annotation { "Feature Type Name" : "Feature", "Feature Type Description" : "" }
export const myFeature = defineFeature(function(context is Context, id is Id, definition is map)
    precondition{}
    {
        {
            var Q0;
            Q0=qCreatedBy(makeId("Top.planeOp"),FACE);
            var sketch = newSketch(context, id + "F0", { "sketchPlane" : qUnion([Q0])});
            skCircle(sketch, "E0", {"center": v(0, 0) * mm, "radius": 38.1 * mm});
            skSolve(sketch);
        }
        {
            var Q0;
            Q0 = qSketchRegion(id + "F0", true);
            extrude(context, id + "F1", {"entities" : qUnion([Q0]), "oppositeDirection" : true, "depth" : 3.8 * mm});
        }
        {
            var Q0;
            Q0=makeQuery(id+"F0.imprint","IMPRINT",FACE,{"disambiguationData":[TD([[makeQuery(id+"F0.imprint","IMPRINT",EDGE,{"derivedFrom":sQuery(id+"F0.wireOp",EDGE,"E0")}),1.0]])]});
            var sketch = newSketch(context, id + "F2", { "sketchPlane" : qUnion([Q0])});
            skLineSegment(sketch, "E1", {"start": v(0, 0) * mm, "end": v(0, -3.81) * mm});
            skLineSegment(sketch, "E2", {"start": v(0, -3.81) * mm, "end": v(-5.08, -8.9) * mm});
            skLineSegment(sketch, "E3", {"start": v(-5.08, -8.9) * mm, "end": v(-8.46, -8.9) * mm});
            skLineSegment(sketch, "E4", {"start": v(-20.32, -8.9) * mm, "end": v(-25.4, -3.81) * mm});
            skLineSegment(sketch, "E5", {"start": v(-25.4, -3.81) * mm, "end": v(-25.4, 0) * mm});
            skLineSegment(sketch, "E6", {"start": v(-25.4, 0) * mm, "end": v(-25.4, 11.43) * mm});
            skLineSegment(sketch, "E7", {"start": v(-25.4, 11.43) * mm, "end": v(-20.32, 16.5) * mm});
            skLineSegment(sketch, "E8", {"start": v(-20.32, 16.5) * mm, "end": v(-5.08, 16.5) * mm});
            skLineSegment(sketch, "E9", {"start": v(-5.08, 16.5) * mm, "end": v(0, 11.43) * mm});
            skLineSegment(sketch, "E10", {"start": v(0, 11.43) * mm, "end": v(0, 7.62) * mm});
            skLineSegment(sketch, "E11", {"start": v(0, 7.62) * mm, "end": v(-5.08, 7.62) * mm});
            skLineSegment(sketch, "E12", {"start": v(-5.08, 7.62) * mm, "end": v(-5.08, 11.43) * mm});
            skLineSegment(sketch, "E13", {"start": v(-5.08, 11.43) * mm, "end": v(-20.32, 11.43) * mm});
            skLineSegment(sketch, "E14", {"start": v(-20.32, 11.43) * mm, "end": v(-20.32, -3.81) * mm});
            skLineSegment(sketch, "E15", {"start": v(-20.32, -3.81) * mm, "end": v(-13.97, -3.81) * mm});
            skLineSegment(sketch, "E16", {"start": v(-5.08, -3.81) * mm, "end": v(-5.08, 0) * mm});
            skLineSegment(sketch, "E17", {"start": v(-5.08, 0) * mm, "end": v(0, 0) * mm});
            skLineSegment(sketch, "E18", {"start": v(-8.9, 5.08) * mm, "end": v(-13.97, 5.08) * mm});
            skLineSegment(sketch, "E19", {"start": v(-17.78, 5.08) * mm, "end": v(-17.78, 0) * mm});
            skLineSegment(sketch, "E20", {"start": v(-17.78, 0) * mm, "end": v(-13.97, 0) * mm});
            skLineSegment(sketch, "E21", {"start": v(-13.97, 0) * mm, "end": v(-13.97, -3.81) * mm});
            skLineSegment(sketch, "E22", {"start": v(-8.9, 5.08) * mm, "end": v(-8.9, -3.81) * mm});
            skLineSegment(sketch, "E23.trimOffspring", {"start": v(-8.9, -3.81) * mm, "end": v(-5.08, -3.81) * mm});
            skLineSegment(sketch, "E24", {"start": v(-8.46, -8.9) * mm, "end": v(-8.46, -16.52) * mm});
            skLineSegment(sketch, "E25", {"start": v(-8.46, -16.52) * mm, "end": v(6.78, -16.52) * mm});
            skLineSegment(sketch, "E26", {"start": v(6.78, -16.52) * mm, "end": v(6.78, 5.07) * mm});
            skLineSegment(sketch, "E27", {"start": v(6.78, 5.07) * mm, "end": v(14.4, 5.07) * mm});
            skLineSegment(sketch, "E28", {"start": v(14.4, 5.07) * mm, "end": v(14.4, 0) * mm});
            skLineSegment(sketch, "E29", {"start": v(14.4, 0) * mm, "end": v(11.86, 0) * mm});
            skLineSegment(sketch, "E30", {"start": v(11.86, 0) * mm, "end": v(11.86, -16.52) * mm});
            skLineSegment(sketch, "E31", {"start": v(11.86, -16.52) * mm, "end": v(6.78, -21.6) * mm});
            skLineSegment(sketch, "E32", {"start": v(6.78, -21.6) * mm, "end": v(-8.46, -21.6) * mm});
            skLineSegment(sketch, "E33", {"start": v(-8.46, -21.6) * mm, "end": v(-13.54, -16.52) * mm});
            skLineSegment(sketch, "E34", {"start": v(-13.54, -16.52) * mm, "end": v(-13.54, -8.9) * mm});
            skLineSegment(sketch, "E35", {"start": v(-13.97, 5.08) * mm, "end": v(-17.78, 5.08) * mm});
            skCircle(sketch, "E36", {"center": v(0, 0) * mm, "radius": 34.93 * mm});
            skLineSegment(sketch, "E37.trimOffspring", {"start": v(-13.54, -8.9) * mm, "end": v(-20.32, -8.9) * mm});
            skText(sketch, "E38", { "text": "P", "fontName": "OpenSans-Regular.ttf"});
            skText(sketch, "E39", { "text": "C", "fontName": "OpenSans-Regular.ttf"});
            skText(sketch, "E40", { "text": "D", "fontName": "OpenSans-Regular.ttf"});
            skText(sketch, "E41", { "text": "P\n", "fontName": "OpenSans-Regular.ttf"});
            const initialGuessF2  = {"E38": [0.00385, 0.01917, 1, 0, 0.00762], "E39": [0.00554, 0.0141, 1, 0, 0.00762], "E40": [0.0099, 0.00647, 1, 0, 0.00762], "E41": [0.0139, -0.00203, 1, 0, 0.00762]};
            skSetInitialGuess(sketch, initialGuessF2);
            skSolve(sketch);
        }
        {
            var Q0;
            Q0=makeQuery(id+"F2.imprint","IMPRINT",FACE,{"disambiguationData":[TD([[makeQuery(id+"F2.imprint","IMPRINT",EDGE,{"derivedFrom":sQuery(id+"F2.wireOp",EDGE,"E36")}),-1.0]])]});
            var Q1;
            Q1=makeQuery(id+"F2.imprint","IMPRINT",FACE,{"disambiguationData":[TD([[makeQuery(id+"F2.imprint","IMPRINT",EDGE,{"derivedFrom":sQuery(id+"F2.wireOp",EDGE,"E1")}),-1.0]])]});
            var Q2;
            Q2=makeQuery(id+"F2.imprint","IMPRINT",FACE,{"disambiguationData":[TD([[makeQuery(id+"F2.imprint","IMPRINT",EDGE,{"derivedFrom":sQuery(id+"F2.wireOp",EDGE,"E38.sketch_text.stroke-0")}),-1.0]])]});
            var Q3;
            Q3=makeQuery(id+"F2.imprint","IMPRINT",FACE,{"disambiguationData":[TD([[makeQuery(id+"F2.imprint","IMPRINT",EDGE,{"derivedFrom":sQuery(id+"F2.wireOp",EDGE,"E39.sketch_text.stroke-0")}),-1.0]])]});
            var Q4;
            Q4=makeQuery(id+"F2.imprint","IMPRINT",FACE,{"disambiguationData":[TD([[makeQuery(id+"F2.imprint","IMPRINT",EDGE,{"derivedFrom":sQuery(id+"F2.wireOp",EDGE,"E40.sketch_text.stroke-0")}),-1.0]])]});
            var Q5;
            Q5=makeQuery(id+"F2.imprint","IMPRINT",FACE,{"disambiguationData":[TD([[makeQuery(id+"F2.imprint","IMPRINT",EDGE,{"derivedFrom":sQuery(id+"F2.wireOp",EDGE,"E41.sketch_text.stroke-0")}),-1.0]])]});
            extrude(context, id + "F3", {"entities" : qUnion([Q0, Q1, Q2, Q3, Q4, Q5]), "depth" : 0.64 * mm});
        }
        {
            var Q0;
            Q0=makeQuery(id+"F1.opExtrude","CAP_FACE",FACE,{"disambiguationData":[OSD([sQuery(id+"F0.wireOp",EDGE,"E0")])],"isStart":false});
            var sketch = newSketch(context, id + "F4", { "sketchPlane" : qUnion([Q0])});
            skText(sketch, "E42", { "text": "Edi Rivas", "fontName": "OpenSans-Bold.ttf"});
            skText(sketch, "E43", { "text": "2016", "fontName": "OpenSans-Bold.ttf"});
            skCircle(sketch, "E44", {"center": v(0, 0) * mm, "radius": 34.93 * mm});
            const initialGuessF4  = {"E42": [-0.01366, 0.0027, 1, 0, 0.0062], "E43": [-0.0086, -0.009, 1, 0, 0.0079]};
            skSetInitialGuess(sketch, initialGuessF4);
            skSolve(sketch);
        }
        {
            var Q0;
            Q0=makeQuery(id+"F4.imprint","IMPRINT",FACE,{"disambiguationData":[TD([[makeQuery(id+"F4.imprint","IMPRINT",EDGE,{"derivedFrom":sQuery(id+"F4.wireOp",EDGE,"E42.sketch_text.stroke-0")}),-1.0]])]});
            var Q1;
            Q1=makeQuery(id+"F4.imprint","IMPRINT",FACE,{"disambiguationData":[TD([[makeQuery(id+"F4.imprint","IMPRINT",EDGE,{"derivedFrom":sQuery(id+"F4.wireOp",EDGE,"E42.sketch_text.stroke-12")}),-1.0]])]});
            var Q2;
            Q2=makeQuery(id+"F4.imprint","IMPRINT",FACE,{"disambiguationData":[TD([[makeQuery(id+"F4.imprint","IMPRINT",EDGE,{"derivedFrom":sQuery(id+"F4.wireOp",EDGE,"E42.sketch_text.stroke-40")}),-1.0]])]});
            var Q3;
            Q3=makeQuery(id+"F4.imprint","IMPRINT",FACE,{"disambiguationData":[TD([[makeQuery(id+"F4.imprint","IMPRINT",EDGE,{"derivedFrom":sQuery(id+"F4.wireOp",EDGE,"E42.sketch_text.stroke-35")}),-1.0]])]});
            var Q4;
            Q4=makeQuery(id+"F4.imprint","IMPRINT",FACE,{"disambiguationData":[TD([[makeQuery(id+"F4.imprint","IMPRINT",EDGE,{"derivedFrom":sQuery(id+"F4.wireOp",EDGE,"E42.sketch_text.stroke-44")}),-1.0]])]});
            var Q5;
            Q5=makeQuery(id+"F4.imprint","IMPRINT",FACE,{"disambiguationData":[TD([[makeQuery(id+"F4.imprint","IMPRINT",EDGE,{"derivedFrom":sQuery(id+"F4.wireOp",EDGE,"E42.sketch_text.stroke-63")}),-1.0]])]});
            var Q6;
            Q6=makeQuery(id+"F4.imprint","IMPRINT",FACE,{"disambiguationData":[TD([[makeQuery(id+"F4.imprint","IMPRINT",EDGE,{"derivedFrom":sQuery(id+"F4.wireOp",EDGE,"E42.sketch_text.stroke-68")}),-1.0]])]});
            var Q7;
            Q7=makeQuery(id+"F4.imprint","IMPRINT",FACE,{"disambiguationData":[TD([[makeQuery(id+"F4.imprint","IMPRINT",EDGE,{"derivedFrom":sQuery(id+"F4.wireOp",EDGE,"E42.sketch_text.stroke-72")}),-1.0]])]});
            var Q8;
            Q8=makeQuery(id+"F4.imprint","IMPRINT",FACE,{"disambiguationData":[TD([[makeQuery(id+"F4.imprint","IMPRINT",EDGE,{"derivedFrom":sQuery(id+"F4.wireOp",EDGE,"E42.sketch_text.stroke-82")}),-1.0]])]});
            var Q9;
            Q9=makeQuery(id+"F4.imprint","IMPRINT",FACE,{"disambiguationData":[TD([[makeQuery(id+"F4.imprint","IMPRINT",EDGE,{"derivedFrom":sQuery(id+"F4.wireOp",EDGE,"E42.sketch_text.stroke-107")}),-1.0]])]});
            var Q10;
            Q10=makeQuery(id+"F4.imprint","IMPRINT",FACE,{"disambiguationData":[TD([[makeQuery(id+"F4.imprint","IMPRINT",EDGE,{"derivedFrom":sQuery(id+"F4.wireOp",EDGE,"E43.sketch_text.stroke-50")}),-1.0]])]});
            var Q11;
            Q11=makeQuery(id+"F4.imprint","IMPRINT",FACE,{"disambiguationData":[TD([[makeQuery(id+"F4.imprint","IMPRINT",EDGE,{"derivedFrom":sQuery(id+"F4.wireOp",EDGE,"E43.sketch_text.stroke-40")}),-1.0]])]});
            var Q12;
            Q12=makeQuery(id+"F4.imprint","IMPRINT",FACE,{"disambiguationData":[TD([[makeQuery(id+"F4.imprint","IMPRINT",EDGE,{"derivedFrom":sQuery(id+"F4.wireOp",EDGE,"E43.sketch_text.stroke-24")}),-1.0]])]});
            var Q13;
            Q13=makeQuery(id+"F4.imprint","IMPRINT",FACE,{"disambiguationData":[TD([[makeQuery(id+"F4.imprint","IMPRINT",EDGE,{"derivedFrom":sQuery(id+"F4.wireOp",EDGE,"E43.sketch_text.stroke-0")}),-1.0]])]});
            var Q14;
            Q14=makeQuery(id+"F4.imprint","IMPRINT",FACE,{"disambiguationData":[TD([[makeQuery(id+"F4.imprint","IMPRINT",EDGE,{"derivedFrom":sQuery(id+"F4.wireOp",EDGE,"E44")}),-1.0]])]});
            extrude(context, id + "F5", {"entities" : qUnion([Q0, Q1, Q2, Q3, Q4, Q5, Q6, Q7, Q8, Q9, Q10, Q11, Q12, Q13, Q14]), "operationType" : NewBodyOperationType.ADD, "depth" : 0.64 * mm});
        }
        {
            var Q0;
            Q0 = qSketchRegion(id + "F2", true);
            var Q1;
            Q1=makeQuery(id+"F0.imprint","IMPRINT",FACE,{"disambiguationData":[TD([[makeQuery(id+"F0.imprint","IMPRINT",EDGE,{"derivedFrom":sQuery(id+"F0.wireOp",EDGE,"E0")}),1.0]])]});
            extrude(context, id + "F6", {"entities" : qUnion([Q0, Q1]), "operationType" : NewBodyOperationType.ADD, "oppositeDirection" : true, "depth" : 0.64 * mm});
        }
    });